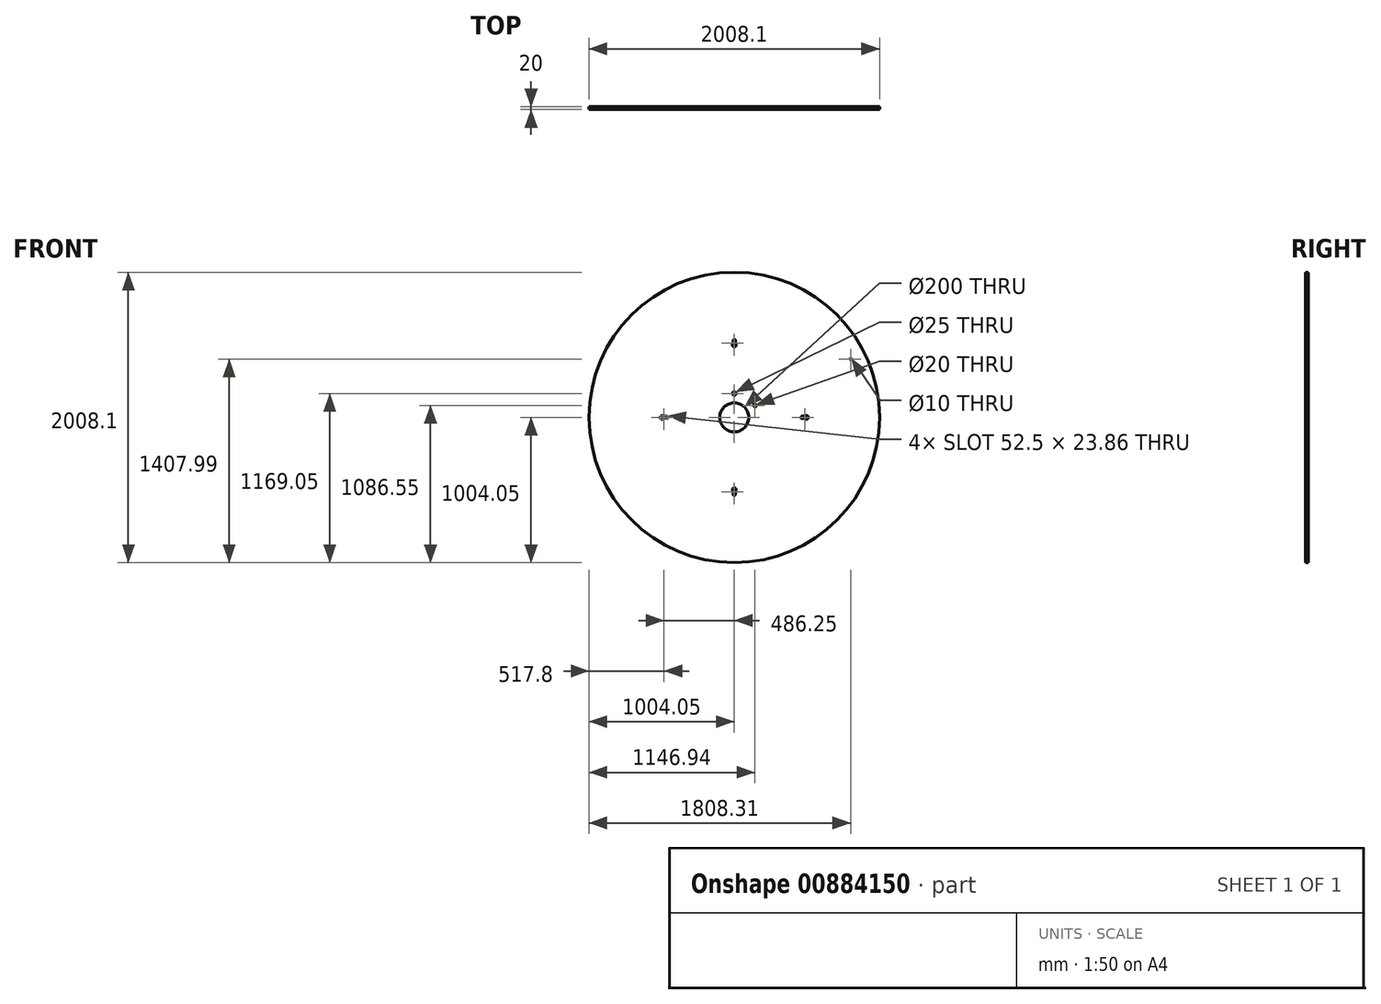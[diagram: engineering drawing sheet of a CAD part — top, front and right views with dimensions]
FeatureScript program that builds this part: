
annotation { "Feature Type Name" : "Feature", "Feature Type Description" : "" }
export const myFeature = defineFeature(function(context is Context, id is Id, definition is map)
    precondition{}
    {
        {
            var Q0;
            Q0=qCreatedBy(makeId("Front.planeOp"),FACE);
            var sketch = newSketch(context, id + "F0", { "sketchPlane" : qUnion([Q0])});
            skCircle(sketch, "E0", {"center": v(0, 0) * mm, "radius": 1004.05 * mm});
            skCircle(sketch, "E1", {"center": v(0, 0) * mm, "radius": 100 * mm});
            skCircle(sketch, "E2", {"center": v(0, 0) * mm, "radius": 165 * mm, "construction": true});
            skLineSegment(sketch, "E3.anchor1", {"start": v(0, 0) * mm, "end": v(0, 165) * mm, "construction": true});
            skLineSegment(sketch, "E3.anchor2", {"start": v(0, 0) * mm, "end": v(0, 165) * mm, "construction": true});
            skPoint(sketch, "E4", {"position": v(0, 165) * mm});
            skLineSegment(sketch, "E5", {"start": v(0, 0) * mm, "end": v(142.9, 82.5) * mm, "construction": true});
            skPoint(sketch, "E6", {"position": v(142.9, 82.5) * mm});
            skCircle(sketch, "E7", {"center": v(0, 0) * mm, "radius": 900 * mm, "construction": true});
            skPoint(sketch, "E8", {"position": v(804.26, 403.94) * mm});
            skCircle(sketch, "E9", {"center": v(0, 0) * mm, "radius": 500 * mm, "construction": true});
            skCircle(sketch, "E10", {"center": v(0, 500) * mm, "radius": 12.5 * mm});
            skLineSegment(sketch, "E11.bottom", {"start": v(-7.5, 505.43) * mm, "end": v(7.5, 505.43) * mm});
            skLineSegment(sketch, "E11.top", {"start": v(0, 540) * mm, "end": v(0, 540) * mm});
            skLineSegment(sketch, "E11.left", {"start": v(-7.5, 505.43) * mm, "end": v(-7.5, 532.5) * mm});
            skLineSegment(sketch, "E11.right", {"start": v(7.5, 505.43) * mm, "end": v(7.5, 532.5) * mm});
            skPoint(sketch, "E12.visualSharp", {"position": v(-7.5, 540) * mm});
            skArc(sketch, "E12.filletArc", {"start": v(0, 540) * mm, "mid": v(-5.3, 537.8) * mm, "end": v(-7.5, 532.5) * mm});
            skPoint(sketch, "E13.visualSharp", {"position": v(7.5, 540) * mm});
            skArc(sketch, "E13.filletArc", {"start": v(7.5, 532.5) * mm, "mid": v(5.3, 537.8) * mm, "end": v(0, 540) * mm});
            skPoint(sketch, "E14.1.0", {"position": v(-540, 7.5) * mm});
            skLineSegment(sketch, "E14.1.1", {"start": v(-494.57, 7.5) * mm, "end": v(-467.5, 7.5) * mm});
            skPoint(sketch, "E14.1.2", {"position": v(-540, -7.5) * mm});
            skCircle(sketch, "E14.1.3", {"center": v(-500, 0) * mm, "radius": 12.5 * mm});
            skLineSegment(sketch, "E14.1.4", {"start": v(-494.57, -7.5) * mm, "end": v(-467.5, -7.5) * mm});
            skLineSegment(sketch, "E14.1.5", {"start": v(-494.57, 7.5) * mm, "end": v(-494.57, -7.5) * mm});
            skArc(sketch, "E14.1.6", {"start": v(-460, 0) * mm, "mid": v(-462.2, 5.3) * mm, "end": v(-467.5, 7.5) * mm});
            skArc(sketch, "E14.1.7", {"start": v(-467.5, -7.5) * mm, "mid": v(-462.2, -5.3) * mm, "end": v(-460, 0) * mm});
            skPoint(sketch, "E14.2.0", {"position": v(-7.5, -540) * mm});
            skLineSegment(sketch, "E14.2.1", {"start": v(7.5, -505.43) * mm, "end": v(7.5, -532.5) * mm});
            skPoint(sketch, "E14.2.2", {"position": v(7.5, -540) * mm});
            skCircle(sketch, "E14.2.3", {"center": v(0, -500) * mm, "radius": 12.5 * mm});
            skLineSegment(sketch, "E14.2.4", {"start": v(-7.5, -505.43) * mm, "end": v(-7.5, -532.5) * mm});
            skLineSegment(sketch, "E14.2.5", {"start": v(7.5, -505.43) * mm, "end": v(-7.5, -505.43) * mm});
            skArc(sketch, "E14.2.6", {"start": v(0, -540) * mm, "mid": v(5.3, -537.8) * mm, "end": v(7.5, -532.5) * mm});
            skArc(sketch, "E14.2.7", {"start": v(-7.5, -532.5) * mm, "mid": v(-5.3, -537.8) * mm, "end": v(0, -540) * mm});
            skPoint(sketch, "E14.3.0", {"position": v(540, -7.5) * mm});
            skLineSegment(sketch, "E14.3.1", {"start": v(494.57, -7.5) * mm, "end": v(467.5, -7.5) * mm});
            skPoint(sketch, "E14.3.2", {"position": v(540, 7.5) * mm});
            skCircle(sketch, "E14.3.3", {"center": v(500, 0) * mm, "radius": 12.5 * mm});
            skLineSegment(sketch, "E14.3.4", {"start": v(494.57, 7.5) * mm, "end": v(467.5, 7.5) * mm});
            skLineSegment(sketch, "E14.3.5", {"start": v(494.57, -7.5) * mm, "end": v(494.57, 7.5) * mm});
            skArc(sketch, "E14.3.6", {"start": v(460, 0) * mm, "mid": v(462.2, -5.3) * mm, "end": v(467.5, -7.5) * mm});
            skArc(sketch, "E14.3.7", {"start": v(467.5, 7.5) * mm, "mid": v(462.2, 5.3) * mm, "end": v(460, 0) * mm});
            skSolve(sketch);
        }
        {
            var Q0;
            Q0=makeQuery(id+"F0.imprint","IMPRINT",FACE,{"disambiguationData":[TD([[makeQuery(id+"F0.imprint","IMPRINT",EDGE,{"derivedFrom":sQuery(id+"F0.wireOp",EDGE,"E0")}),1.0]])]});
            extrude(context, id + "F1", {"entities" : qUnion([Q0]), "oppositeDirection" : true, "depth" : 20 * mm, "offsetDistance" : 25 * mm});
        }
        {
            var Q0;
            Q0=sQuery(id+"F0.wireOp",VERTEX,"E4");
            var Q1;
            Q1=makeQuery(id+"F1.opExtrude","SWEPT_BODY",BODY,{"disambiguationData":[OSD([sQuery(id+"F0.wireOp",EDGE,"E0"),sQuery(id+"F0.wireOp",EDGE,"E1")])]});
            hole(context, id + "F2", {"style" : HoleStyle.SIMPLE, "endStyle" : HoleEndStyle.BLIND, "holeDiameter" : 25 * mm, "majorDiameter" : 5 * mm, "holeDepth" : 28 * mm, "isTappedThrough" : true, "tappedDepth" : 12 * mm, "tapClearance" : 3, "locations" : qUnion([Q0]), "scope" : qUnion([Q1])});
        }
        {
            var Q0;
            Q0=sQuery(id+"F0.wireOp",VERTEX,"E6");
            var Q1;
            Q1=makeQuery(id+"F1.opExtrude","SWEPT_BODY",BODY,{"disambiguationData":[OSD([sQuery(id+"F0.wireOp",EDGE,"E0"),sQuery(id+"F0.wireOp",EDGE,"E1")])]});
            hole(context, id + "F3", {"style" : HoleStyle.SIMPLE, "endStyle" : HoleEndStyle.BLIND, "holeDiameter" : 20 * mm, "majorDiameter" : 5 * mm, "holeDepth" : 28 * mm, "isTappedThrough" : true, "tappedDepth" : 12 * mm, "tapClearance" : 3, "locations" : qUnion([Q0]), "scope" : qUnion([Q1])});
        }
        {
            var Q0;
            Q0=sQuery(id+"F0.wireOp",VERTEX,"E8");
            var Q1;
            Q1=makeQuery(id+"F1.opExtrude","SWEPT_BODY",BODY,{"disambiguationData":[OSD([sQuery(id+"F0.wireOp",EDGE,"E0"),sQuery(id+"F0.wireOp",EDGE,"E1")])]});
            hole(context, id + "F4", {"style" : HoleStyle.SIMPLE, "endStyle" : HoleEndStyle.BLIND, "holeDiameter" : 10 * mm, "majorDiameter" : 5 * mm, "holeDepth" : 28 * mm, "isTappedThrough" : true, "tappedDepth" : 12 * mm, "tapClearance" : 3, "locations" : qUnion([Q0]), "scope" : qUnion([Q1])});
        }
    });
